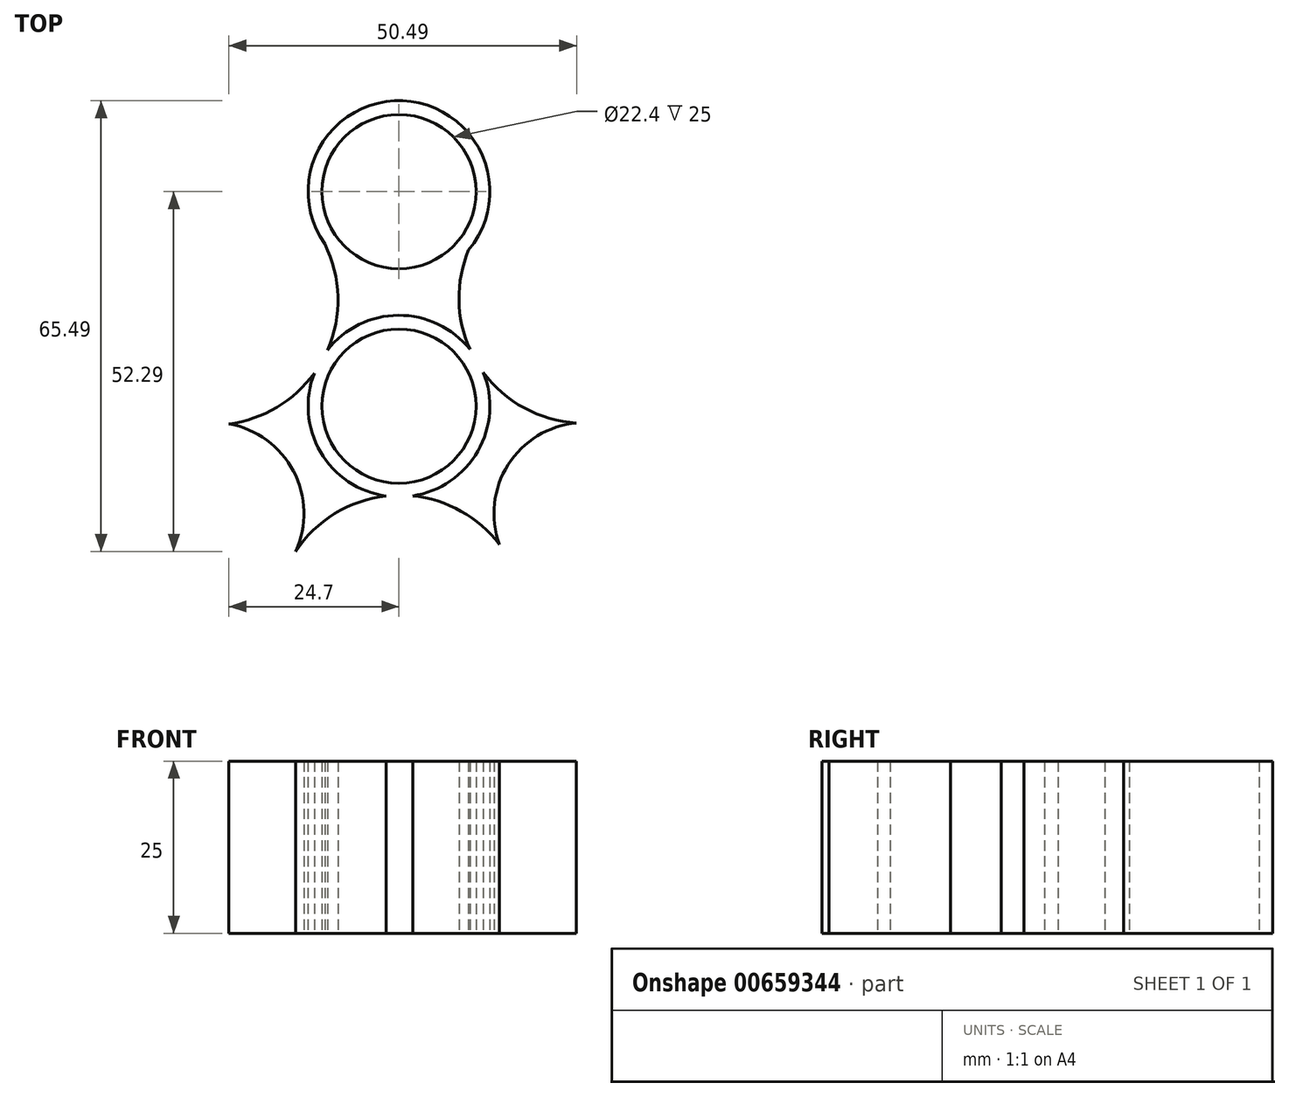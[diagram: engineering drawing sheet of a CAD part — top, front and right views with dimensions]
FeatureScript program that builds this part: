
annotation { "Feature Type Name" : "Feature", "Feature Type Description" : "" }
export const myFeature = defineFeature(function(context is Context, id is Id, definition is map)
    precondition{}
    {
        {
            var Q0;
            Q0=qCreatedBy(makeId("Top.planeOp"),FACE);
            var sketch = newSketch(context, id + "F0", { "sketchPlane" : qUnion([Q0])});
            skCircle(sketch, "E0", {"center": v(0, 0) * mm, "radius": 11.2 * mm});
            skCircle(sketch, "E1", {"center": v(0, 0) * mm, "radius": 13.2 * mm});
            skCircle(sketch, "E2", {"center": v(0, 31.18) * mm, "radius": 11.2 * mm});
            skCircle(sketch, "E3", {"center": v(0, 31.18) * mm, "radius": 13.2 * mm});
            skCircle(sketch, "E4.1.0", {"center": v(-27, -15.59) * mm, "radius": 11.2 * mm});
            skCircle(sketch, "E4.1.1", {"center": v(-27, -15.59) * mm, "radius": 13.2 * mm});
            skCircle(sketch, "E4.2.0", {"center": v(27, -15.59) * mm, "radius": 11.2 * mm});
            skCircle(sketch, "E4.2.1", {"center": v(27, -15.59) * mm, "radius": 13.2 * mm});
            skArc(sketch, "E5", {"start": v(10.1, 22.69) * mm, "mid": v(11.46, 6.08) * mm, "end": v(25.79, -2.45) * mm});
            skArc(sketch, "E6.1.0", {"start": v(-24.7, -2.6) * mm, "mid": v(-11, 6.89) * mm, "end": v(-10.77, 23.55) * mm});
            skArc(sketch, "E6.2.0", {"start": v(14.6, -20.1) * mm, "mid": v(-0.47, -12.97) * mm, "end": v(-15.01, -21.1) * mm});
            skSolve(sketch);
        }
        {
            var Q0;
            Q0=qCreatedBy(makeId("Top.planeOp"),FACE);
            var sketch = newSketch(context, id + "F1", { "sketchPlane" : qUnion([Q0])});
            skSolve(sketch);
        }
        {
            var Q0;
            Q0 = qSketchRegion(id + "F1", true);
            var Q1;
            Q1=makeQuery(id+"F0.imprint","IMPRINT",FACE,{"disambiguationData":[TD([[makeQuery(id+"F0.imprint","IMPRINT",EDGE,{"derivedFrom":sQuery(id+"F0.wireOp",EDGE,"E2")}),-1.0]])]});
            var Q2;
            {var subQ0=sQuery(id+"F0.wireOp",EDGE,"E6.1.0");var subQ1=sQuery(id+"F0.wireOp",EDGE,"E1");var subQ2=makeQuery(id+"F0.imprint","INTERSECT",VERTEX,{"disambiguationData":[OD(1.0)],"derivedFrom":[subQ1,subQ0]});Q2=makeQuery(id+"F0.imprint","IMPRINT",FACE,{"disambiguationData":[TD([[makeQuery(id+"F0.imprint","IMPRINT",EDGE,{"disambiguationData":[TD([[subQ2,-1.0]])],"derivedFrom":subQ1}),-1.0]])]});}
            var Q3;
            {var subQ0=sQuery(id+"F0.wireOp",EDGE,"E5");var subQ1=sQuery(id+"F0.wireOp",EDGE,"E1");var subQ2=makeQuery(id+"F0.imprint","INTERSECT",VERTEX,{"disambiguationData":[OD(0.0)],"derivedFrom":[subQ1,subQ0]});Q3=makeQuery(id+"F0.imprint","IMPRINT",FACE,{"disambiguationData":[TD([[makeQuery(id+"F0.imprint","IMPRINT",EDGE,{"disambiguationData":[TD([[subQ2,-1.0]])],"derivedFrom":subQ1}),-1.0]])]});}
            var Q4;
            Q4=makeQuery(id+"F0.imprint","IMPRINT",FACE,{"disambiguationData":[TD([[makeQuery(id+"F0.imprint","IMPRINT",EDGE,{"derivedFrom":sQuery(id+"F0.wireOp",EDGE,"E0")}),1.0]])]});
            var Q5;
            {var subQ0=sQuery(id+"F0.wireOp",EDGE,"E5");var subQ1=sQuery(id+"F0.wireOp",EDGE,"E1");var subQ2=makeQuery(id+"F0.imprint","INTERSECT",VERTEX,{"disambiguationData":[OD(1.0)],"derivedFrom":[subQ1,subQ0]});Q5=makeQuery(id+"F0.imprint","IMPRINT",FACE,{"disambiguationData":[TD([[makeQuery(id+"F0.imprint","IMPRINT",EDGE,{"disambiguationData":[TD([[subQ2,1.0]])],"derivedFrom":subQ1}),-1.0]])]});}
            extrude(context, id + "F2", {"entities" : qUnion([Q0, Q1, Q2, Q3, Q4, Q5]), "depth" : 25 * mm, "offsetDistance" : 25 * mm});
        }
    });
